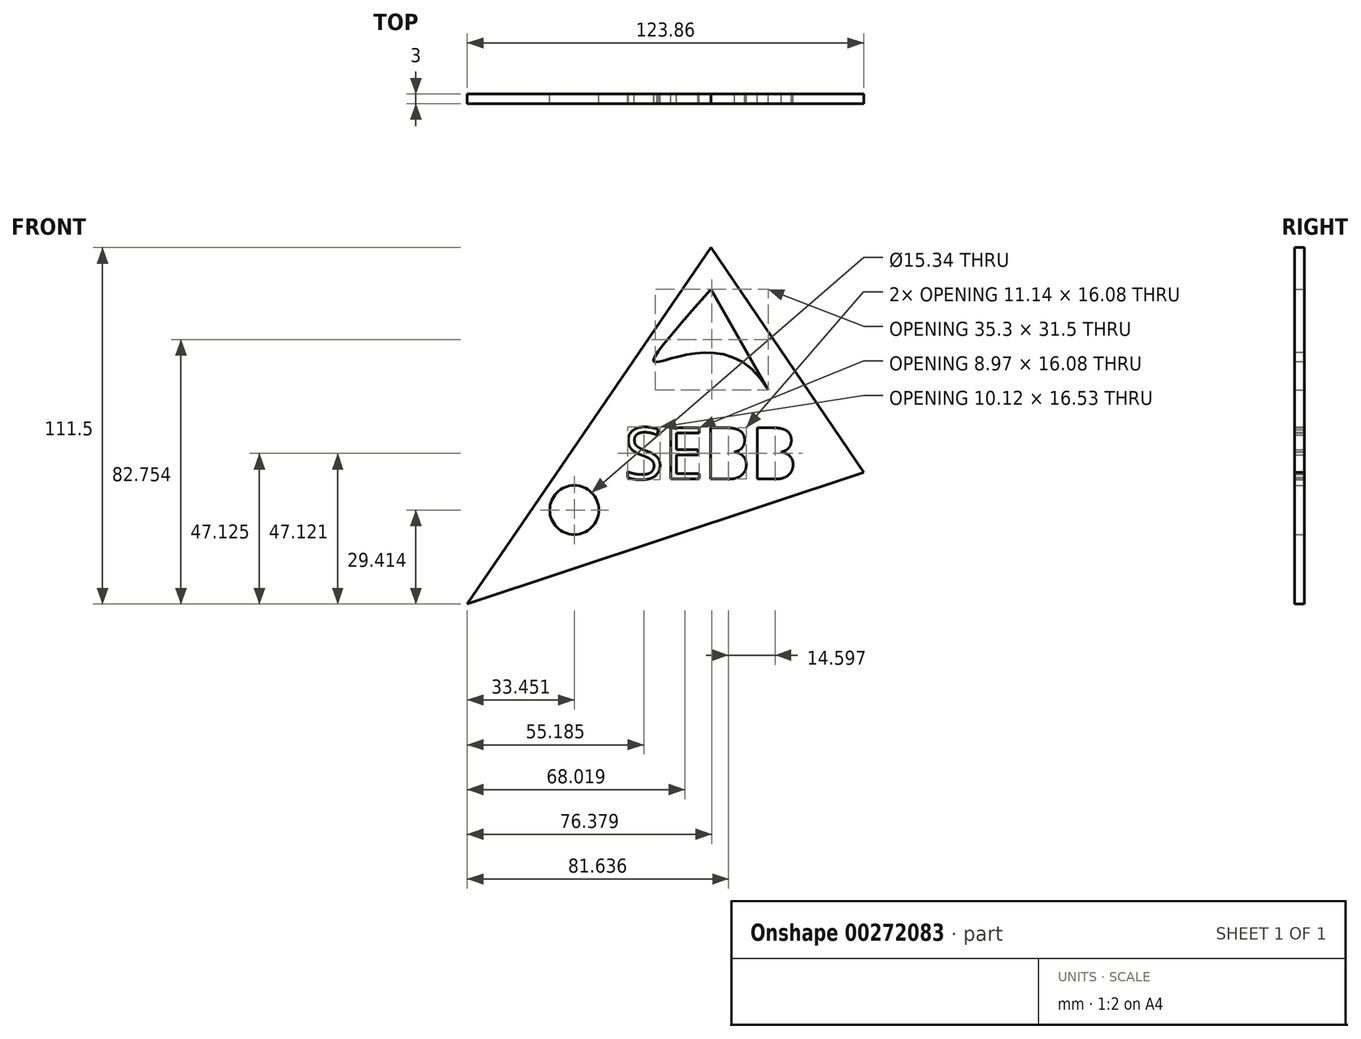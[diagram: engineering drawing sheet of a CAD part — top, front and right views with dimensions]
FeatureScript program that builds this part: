
annotation { "Feature Type Name" : "Feature", "Feature Type Description" : "" }
export const myFeature = defineFeature(function(context is Context, id is Id, definition is map)
    precondition{}
    {
        {
            var Q0;
            Q0=qCreatedBy(makeId("Front.planeOp"),FACE);
            var sketch = newSketch(context, id + "F0", { "sketchPlane" : qUnion([Q0])});
            skLineSegment(sketch, "E0", {"start": v(0, 56.2) * mm, "end": v(-76.1, -55.3) * mm});
            skLineSegment(sketch, "E1", {"start": v(0, 56.2) * mm, "end": v(47.75, -14.12) * mm});
            skText(sketch, "E2", { "text": "SEBB", "fontName": "OpenSans-Regular.ttf"});
            skLineSegment(sketch, "E3", {"start": v(-76.1, -55.3) * mm, "end": v(47.75, -14.12) * mm});
            skFitSpline(sketch, "E4", {"points": [v(0, 43.2) * mm, v(17.92, 11.7) * mm], "startDerivative": vector(-125.1, -144.3) * mm, "endDerivative": vector(53.75, -94.5) * mm});
            skLineSegment(sketch, "E5", {"start": v(0, 43.2) * mm, "end": v(17.92, 11.7) * mm});
            skCircle(sketch, "E6", {"center": v(-42.66, -25.89) * mm, "radius": 7.67 * mm});
            const initialGuessF0  = {"E2": [-0.02715, -0.01622, 1, 0, 0.01622]};
            skSetInitialGuess(sketch, initialGuessF0);
            skSolve(sketch);
        }
        {
            var Q0;
            Q0 = qSketchRegion(id + "F0", true);
            extrude(context, id + "F1", {"entities" : qUnion([Q0]), "depth" : 3 * mm});
        }
    });
